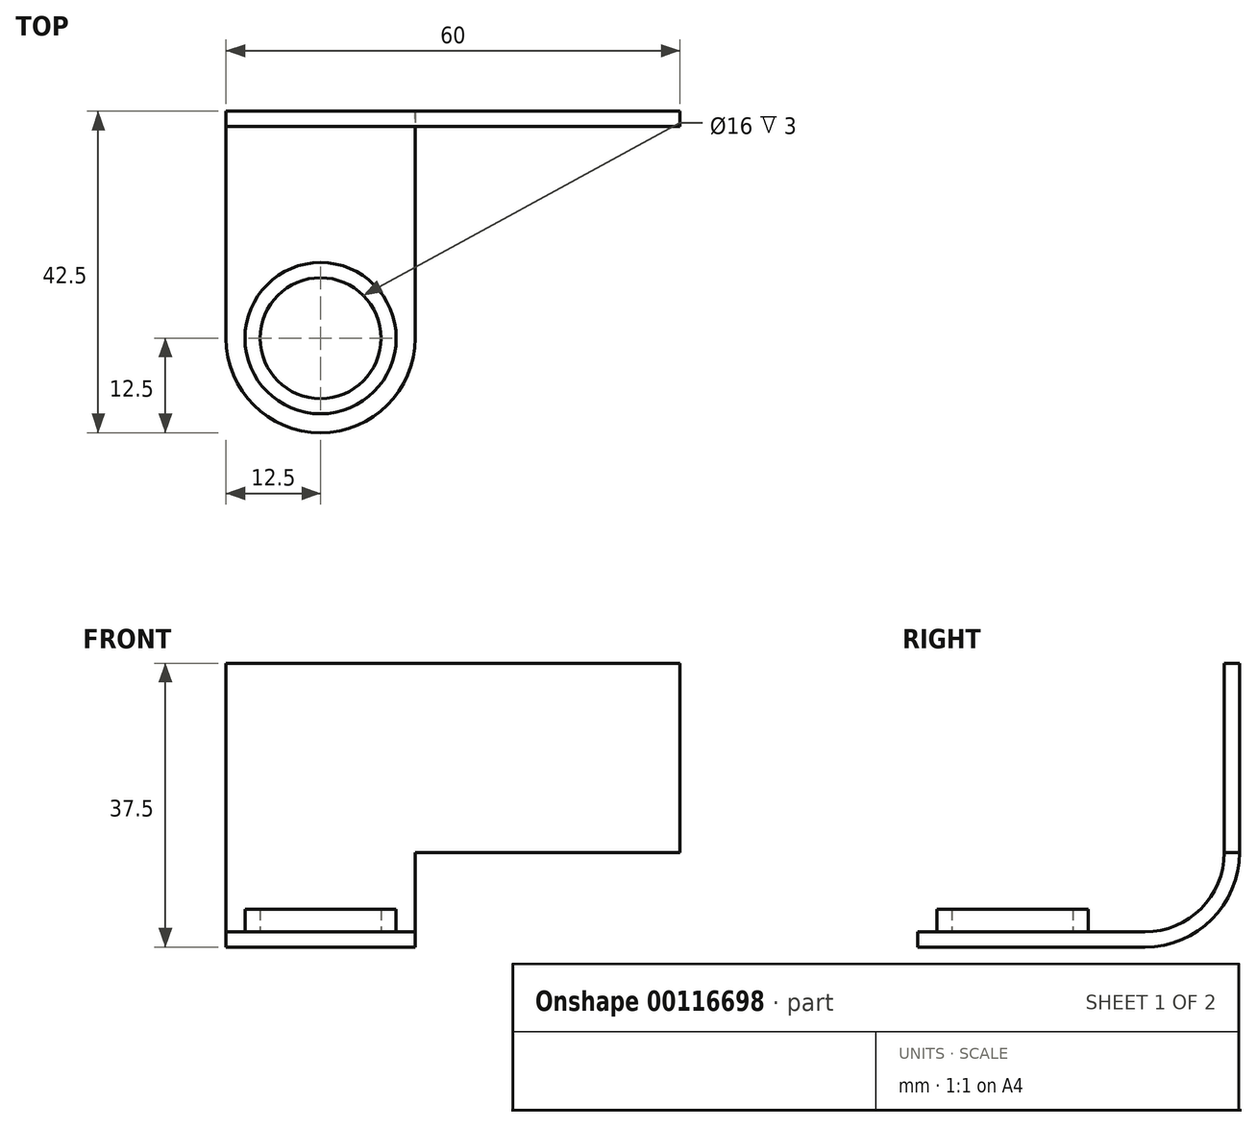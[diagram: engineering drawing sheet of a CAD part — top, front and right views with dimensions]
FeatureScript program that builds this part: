
annotation { "Feature Type Name" : "Feature", "Feature Type Description" : "" }
export const myFeature = defineFeature(function(context is Context, id is Id, definition is map)
    precondition{}
    {
        {
            var Q0;
            Q0=qCreatedBy(makeId("Front.planeOp"),FACE);
            var sketch = newSketch(context, id + "F0", { "sketchPlane" : qUnion([Q0])});
            skLineSegment(sketch, "E0.bottom", {"start": v(-12.5, 0) * mm, "end": v(47.5, 0) * mm});
            skLineSegment(sketch, "E0.top", {"start": v(-12.5, 25) * mm, "end": v(47.5, 25) * mm});
            skLineSegment(sketch, "E0.left", {"start": v(-12.5, 0) * mm, "end": v(-12.5, 25) * mm});
            skLineSegment(sketch, "E0.right", {"start": v(47.5, 0) * mm, "end": v(47.5, 25) * mm});
            skLineSegment(sketch, "E1", {"start": v(0, 0) * mm, "end": v(0, 38.04) * mm, "construction": true});
            skSolve(sketch);
        }
        {
            var Q0;
            Q0 = qSketchRegion(id + "F0", true);
            extrude(context, id + "F1", {"entities" : qUnion([Q0]), "depth" : 2 * mm});
        }
        {
            var Q0;
            Q0=qCreatedBy(makeId("Right.planeOp"),FACE);
            var sketch = newSketch(context, id + "F2", { "sketchPlane" : qUnion([Q0])});
            skArc(sketch, "E2", {"start": v(-12.5, -12.5) * mm, "mid": v(-3.66, -8.84) * mm, "end": v(0, 0) * mm});
            skLineSegment(sketch, "E3", {"start": v(-12.5, -12.5) * mm, "end": v(-42.5, -12.5) * mm});
            skLineSegment(sketch, "E4.0", {"start": v(-12.5, -10.5) * mm, "end": v(-42.5, -10.5) * mm});
            skArc(sketch, "E4.1", {"start": v(-12.5, -10.5) * mm, "mid": v(-5.08, -7.42) * mm, "end": v(-2, 0) * mm});
            skLineSegment(sketch, "E5", {"start": v(-42.5, -10.5) * mm, "end": v(-42.5, -12.5) * mm});
            skLineSegment(sketch, "E6", {"start": v(0, 0) * mm, "end": v(-2, 0) * mm});
            skSolve(sketch);
        }
        {
            var Q0;
            Q0 = qSketchRegion(id + "F2", true);
            extrude(context, id + "F3", {"entities" : qUnion([Q0]), "operationType" : NewBodyOperationType.ADD, "endBound" : BoundingType.SYMMETRIC, "depth" : 25 * mm});
        }
        {
            var Q0;
            Q0=makeQuery(id+"F3.opExtrude","CAP_EDGE",EDGE,{"disambiguationData":[OSD([sQuery(id+"F2.wireOp",EDGE,"E5")])],"isStart":true});
            var Q1;
            Q1=makeQuery(id+"F3.opExtrude","CAP_EDGE",EDGE,{"disambiguationData":[OSD([sQuery(id+"F2.wireOp",EDGE,"E5")])],"isStart":false});
            fillet(context, id + "F4", {"entities" : qUnion([Q0, Q1]), "radius" : 12.5 * mm, "tangentPropagation" : true, "allowEdgeOverflow" : false});
        }
        {
            var Q0;
            Q0=makeQuery(id+"F3.opExtrude","SWEPT_FACE",FACE,{"disambiguationData":[OSD([sQuery(id+"F2.wireOp",EDGE,"E4.0")])]});
            var sketch = newSketch(context, id + "F5", { "sketchPlane" : qUnion([Q0])});
            skCircle(sketch, "E7", {"center": v(0, -30) * mm, "radius": 8 * mm});
            skCircle(sketch, "E8.0", {"center": v(0, -30) * mm, "radius": 10 * mm});
            skSolve(sketch);
        }
        {
            var Q0;
            Q0 = qSketchRegion(id + "F5", true);
            extrude(context, id + "F6", {"entities" : qUnion([Q0]), "operationType" : NewBodyOperationType.ADD, "depth" : 3 * mm});
        }
    });
